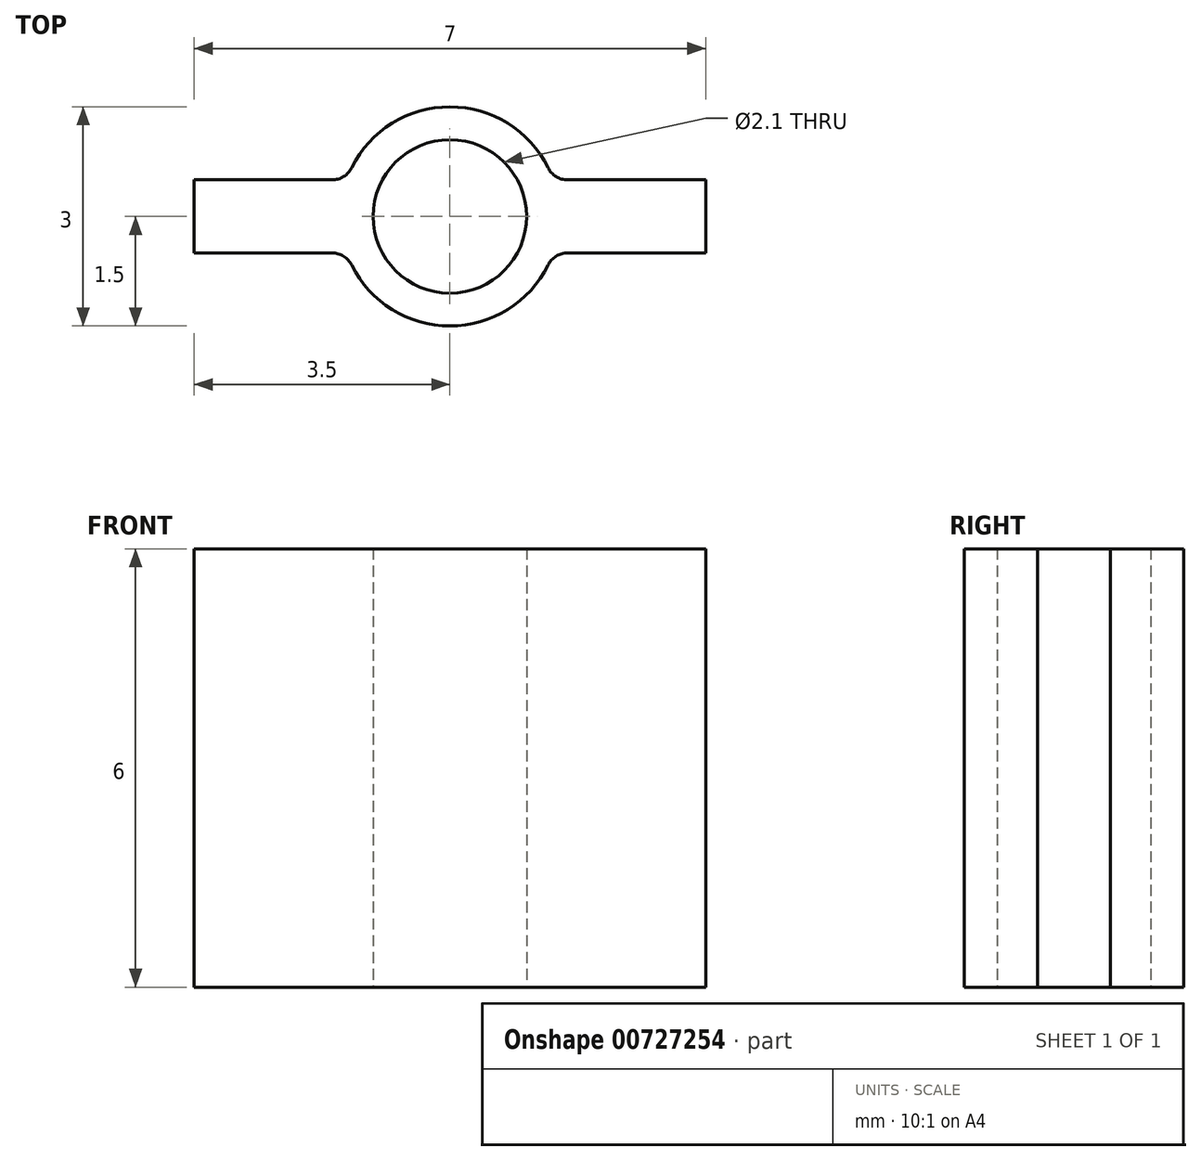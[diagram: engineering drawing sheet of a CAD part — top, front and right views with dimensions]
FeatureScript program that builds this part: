
annotation { "Feature Type Name" : "Feature", "Feature Type Description" : "" }
export const myFeature = defineFeature(function(context is Context, id is Id, definition is map)
    precondition{}
    {
        {
            var Q0;
            Q0=qCreatedBy(makeId("Top.planeOp"),FACE);
            var sketch = newSketch(context, id + "F0", { "sketchPlane" : qUnion([Q0])});
            skLineSegment(sketch, "E0.bottom", {"start": v(-3.5, -0.5) * mm, "end": v(3.5, -0.5) * mm});
            skLineSegment(sketch, "E0.top", {"start": v(-3.5, 0.5) * mm, "end": v(3.5, 0.5) * mm});
            skLineSegment(sketch, "E0.left", {"start": v(-3.5, -0.5) * mm, "end": v(-3.5, 0.5) * mm});
            skLineSegment(sketch, "E0.right", {"start": v(3.5, -0.5) * mm, "end": v(3.5, 0.5) * mm});
            skPoint(sketch, "E0.middle", {"position": v(0, 0) * mm});
            skCircle(sketch, "E1", {"center": v(0, 0) * mm, "radius": 1.5 * mm});
            skCircle(sketch, "E2", {"center": v(0, 0) * mm, "radius": 1.05 * mm});
            skSolve(sketch);
        }
        {
            var Q0;
            Q0 = qSketchRegion(id + "F0", true);
            extrude(context, id + "F1", {"entities" : qUnion([Q0]), "depth" : 6 * mm, "offsetDistance" : 25 * mm});
        }
        {
            var Q0;
            {var subQ0=sQuery(id+"F0.wireOp",EDGE,"E1");var subQ1=sQuery(id+"F0.wireOp",EDGE,"E0.bottom");Q0=makeQuery(id+"F1.opExtrude","SWEPT_EDGE",EDGE,{"disambiguationData":[OSD([subQ1,subQ0]),TDD([makeQuery(id+"F0.imprint","INTERSECT",VERTEX,{"disambiguationData":[OD(1.0)],"derivedFrom":[subQ1,subQ0]})])]});}
            var Q1;
            {var subQ0=sQuery(id+"F0.wireOp",EDGE,"E1");var subQ1=sQuery(id+"F0.wireOp",EDGE,"E0.bottom");Q1=makeQuery(id+"F1.opExtrude","SWEPT_EDGE",EDGE,{"disambiguationData":[OSD([subQ1,subQ0]),TDD([makeQuery(id+"F0.imprint","INTERSECT",VERTEX,{"disambiguationData":[OD(0.0)],"derivedFrom":[subQ1,subQ0]})])]});}
            var Q2;
            {var subQ0=sQuery(id+"F0.wireOp",EDGE,"E1");var subQ1=sQuery(id+"F0.wireOp",EDGE,"E0.top");Q2=makeQuery(id+"F1.opExtrude","SWEPT_EDGE",EDGE,{"disambiguationData":[OSD([subQ1,subQ0]),TDD([makeQuery(id+"F0.imprint","INTERSECT",VERTEX,{"disambiguationData":[OD(1.0)],"derivedFrom":[subQ1,subQ0]})])]});}
            var Q3;
            {var subQ0=sQuery(id+"F0.wireOp",EDGE,"E1");var subQ1=sQuery(id+"F0.wireOp",EDGE,"E0.top");Q3=makeQuery(id+"F1.opExtrude","SWEPT_EDGE",EDGE,{"disambiguationData":[OSD([subQ1,subQ0]),TDD([makeQuery(id+"F0.imprint","INTERSECT",VERTEX,{"disambiguationData":[OD(0.0)],"derivedFrom":[subQ1,subQ0]})])]});}
            fillet(context, id + "F2", {"entities" : qUnion([Q0, Q1, Q2, Q3]), "radius" : 0.3 * mm, "tangentPropagation" : true, "allowEdgeOverflow" : false});
        }
    });
